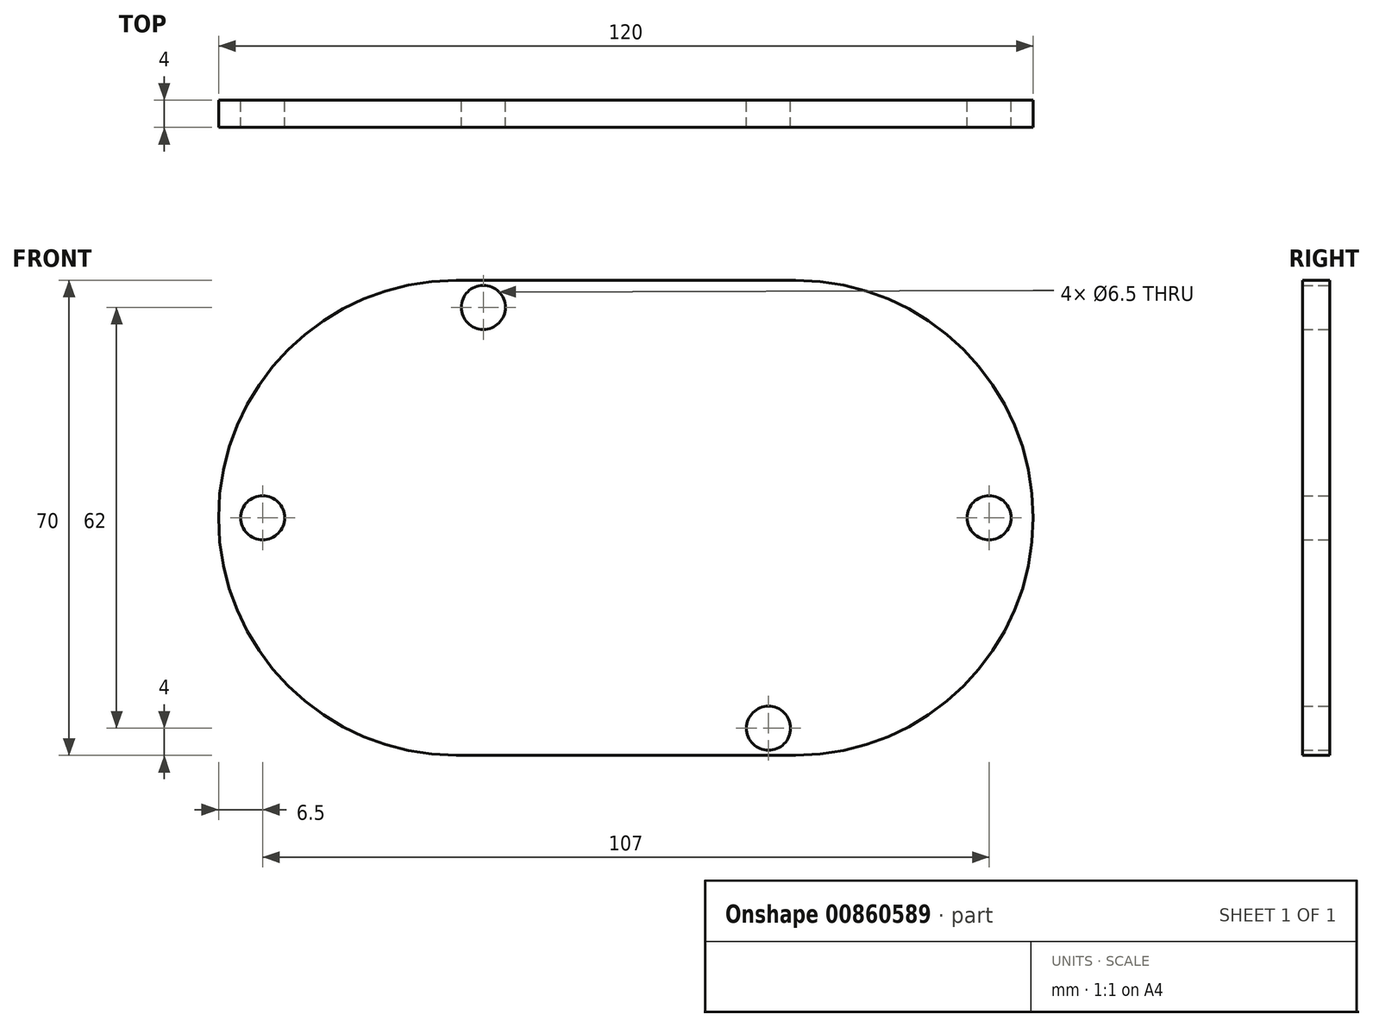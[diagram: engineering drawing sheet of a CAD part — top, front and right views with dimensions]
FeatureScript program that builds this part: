
annotation { "Feature Type Name" : "Feature", "Feature Type Description" : "" }
export const myFeature = defineFeature(function(context is Context, id is Id, definition is map)
    precondition{}
    {
        {
            var Q0;
            Q0=qCreatedBy(makeId("Front.planeOp"),FACE);
            var sketch = newSketch(context, id + "F0", { "sketchPlane" : qUnion([Q0])});
            skLineSegment(sketch, "E0", {"start": v(-25, 35) * mm, "end": v(25, 35) * mm});
            skLineSegment(sketch, "E1", {"start": v(-25, -35) * mm, "end": v(25, -35) * mm});
            skArc(sketch, "E2", {"start": v(25, -35) * mm, "mid": v(60, 0) * mm, "end": v(25, 35) * mm});
            skArc(sketch, "E3", {"start": v(-25, 35) * mm, "mid": v(-60, 0) * mm, "end": v(-25, -35) * mm});
            skSolve(sketch);
        }
        {
            var Q0;
            Q0 = qSketchRegion(id + "F0", true);
            extrude(context, id + "F1", {"entities" : qUnion([Q0]), "depth" : 4 * mm, "offsetDistance" : 25 * mm});
        }
        {
            var Q0;
            Q0=qCreatedBy(makeId("Front.planeOp"),FACE);
            var sketch = newSketch(context, id + "F2", { "sketchPlane" : qUnion([Q0])});
            skCircle(sketch, "E4", {"center": v(-21, 31) * mm, "radius": 3.25 * mm});
            skCircle(sketch, "E5", {"center": v(21, -31) * mm, "radius": 3.25 * mm});
            skCircle(sketch, "E6", {"center": v(53.5, 0) * mm, "radius": 3.25 * mm});
            skCircle(sketch, "E7", {"center": v(-53.5, 0) * mm, "radius": 3.25 * mm});
            skSolve(sketch);
        }
        {
            var Q0;
            Q0 = qSketchRegion(id + "F2", true);
            extrude(context, id + "F3", {"entities" : qUnion([Q0]), "operationType" : NewBodyOperationType.REMOVE, "endBound" : BoundingType.THROUGH_ALL, "depth" : 25 * mm, "offsetDistance" : 25 * mm});
        }
    });
